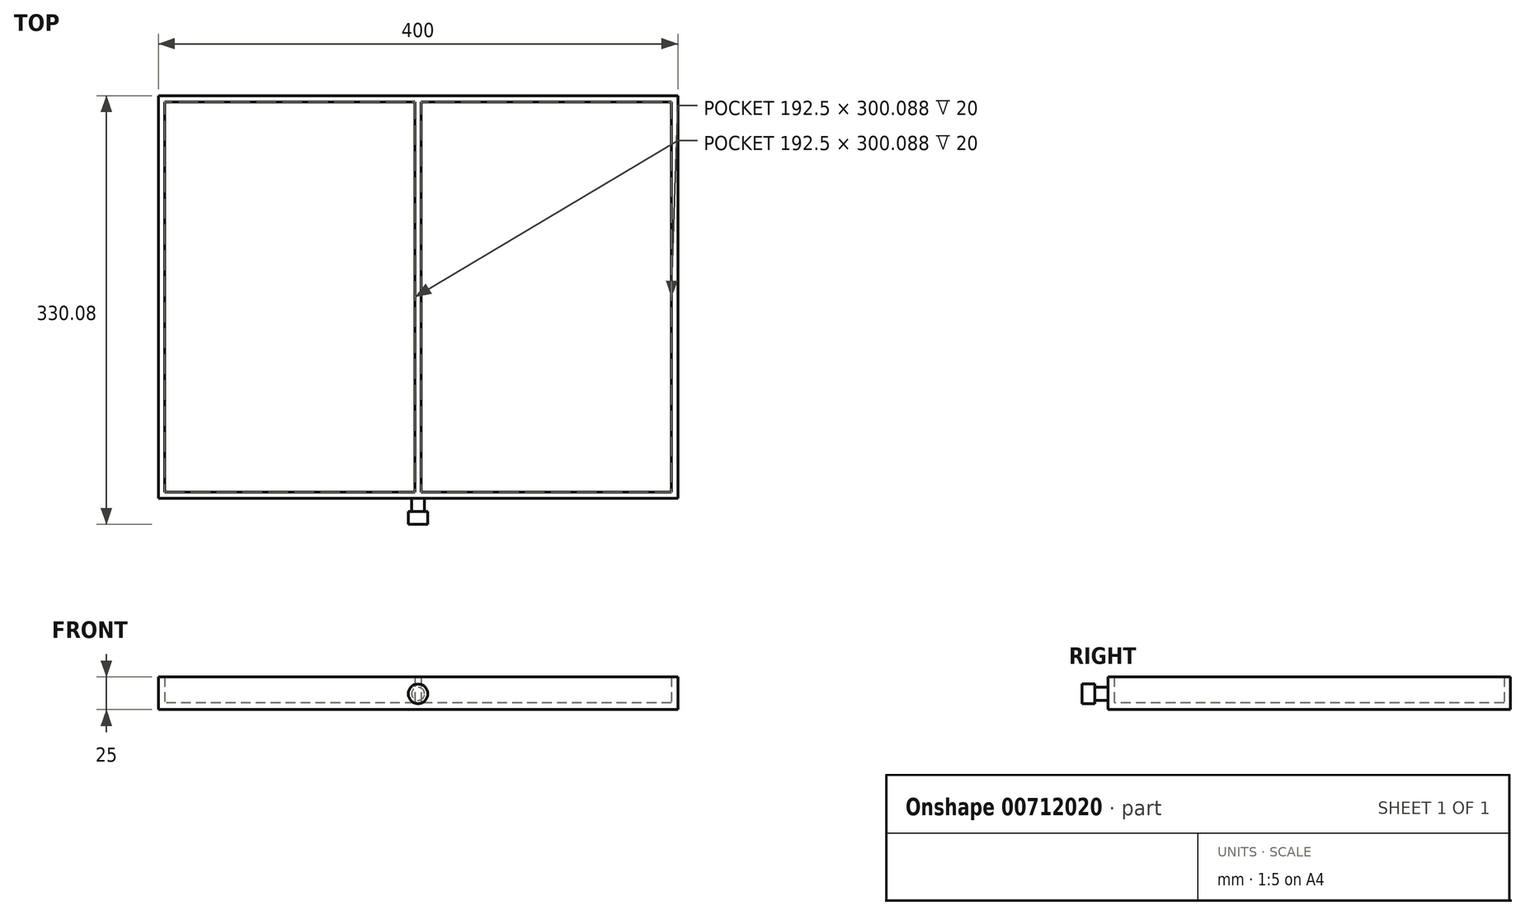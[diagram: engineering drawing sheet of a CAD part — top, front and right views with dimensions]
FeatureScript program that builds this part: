
annotation { "Feature Type Name" : "Feature", "Feature Type Description" : "" }
export const myFeature = defineFeature(function(context is Context, id is Id, definition is map)
    precondition{}
    {
        {
            var Q0;
            Q0=qCreatedBy(makeId("Top.planeOp"),FACE);
            var sketch = newSketch(context, id + "F0", { "sketchPlane" : qUnion([Q0])});
            skLineSegment(sketch, "E0.bottom", {"start": v(-33.22, 0) * mm, "end": v(5.14, 0) * mm});
            skLineSegment(sketch, "E0.top", {"start": v(-33.22, 42.2) * mm, "end": v(5.14, 42.2) * mm});
            skLineSegment(sketch, "E0.left", {"start": v(-33.22, 0) * mm, "end": v(-33.22, 42.2) * mm});
            skLineSegment(sketch, "E0.right", {"start": v(5.14, 0) * mm, "end": v(5.14, 42.2) * mm});
            skSolve(sketch);
        }
        {
            var Q0;
            Q0=makeQuery(id+"F0.imprint","IMPRINT",FACE,{"disambiguationData":[TD([[makeQuery(id+"F0.imprint","IMPRINT",EDGE,{"derivedFrom":sQuery(id+"F0.wireOp",EDGE,"E0.bottom")}),1.0]])]});
            extrude(context, id + "F1", {"entities" : qUnion([Q0]), "depth" : 0.69 * mm, "offsetDistance" : 25.4 * mm});
        }
        {
            var Q0;
            Q0=makeQuery(id+"F1.opExtrude","SWEPT_BODY",BODY,{"disambiguationData":[OSD([sQuery(id+"F0.wireOp",EDGE,"E0.bottom"),sQuery(id+"F0.wireOp",EDGE,"E0.top"),sQuery(id+"F0.wireOp",EDGE,"E0.left"),sQuery(id+"F0.wireOp",EDGE,"E0.right")])]});
            deleteBodies(context, id + "F2", {"entities" : qUnion([Q0])});
        }
        {
            var Q0;
            Q0=qCreatedBy(makeId("Top.planeOp"),FACE);
            var sketch = newSketch(context, id + "F3", { "sketchPlane" : qUnion([Q0])});
            skPoint(sketch, "E1.middle", {"position": v(0, 0) * mm});
            skLineSegment(sketch, "E2.bottom", {"start": v(200, -150.04) * mm, "end": v(-200, -150.04) * mm});
            skLineSegment(sketch, "E2.top", {"start": v(200, 150.04) * mm, "end": v(-200, 150.04) * mm});
            skLineSegment(sketch, "E2.left", {"start": v(200, -150.04) * mm, "end": v(200, 150.04) * mm});
            skLineSegment(sketch, "E2.right", {"start": v(-200, -150.04) * mm, "end": v(-200, 150.04) * mm});
            skSolve(sketch);
        }
        {
            var Q0;
            Q0=qSketchRegion(id+"F3",true);
            extrude(context, id + "F4", {"entities" : qUnion([Q0]), "depth" : 5 * mm, "offsetDistance" : 25 * mm});
        }
        {
            var Q0;
            Q0=makeQuery(id+"F4.opExtrude","CAP_FACE",FACE,{"disambiguationData":[OSD([sQuery(id+"F3.wireOp",EDGE,"E2.bottom"),sQuery(id+"F3.wireOp",EDGE,"E2.top"),sQuery(id+"F3.wireOp",EDGE,"E2.left"),sQuery(id+"F3.wireOp",EDGE,"E2.right")])],"isStart":false});
            var sketch = newSketch(context, id + "F5", { "sketchPlane" : qUnion([Q0])});
            skLineSegment(sketch, "E3.bottom", {"start": v(-200, -150.04) * mm, "end": v(-195, -150.04) * mm});
            skLineSegment(sketch, "E3.top", {"start": v(-200, 150.04) * mm, "end": v(-195, 150.04) * mm});
            skLineSegment(sketch, "E3.left", {"start": v(-200, -150.04) * mm, "end": v(-200, 150.04) * mm});
            skLineSegment(sketch, "E3.right", {"start": v(-195, -150.04) * mm, "end": v(-195, 150.04) * mm});
            skSolve(sketch);
        }
        {
            var Q0;
            Q0=qSketchRegion(id+"F5",true);
            extrude(context, id + "F6", {"entities" : qUnion([Q0]), "operationType" : NewBodyOperationType.ADD, "depth" : 20 * mm, "offsetDistance" : 25 * mm});
        }
        {
            var Q0;
            Q0=makeQuery(id+"F4.opExtrude","CAP_FACE",FACE,{"disambiguationData":[OSD([sQuery(id+"F3.wireOp",EDGE,"E2.bottom"),sQuery(id+"F3.wireOp",EDGE,"E2.top"),sQuery(id+"F3.wireOp",EDGE,"E2.left"),sQuery(id+"F3.wireOp",EDGE,"E2.right")])],"isStart":false});
            var sketch = newSketch(context, id + "F7", { "sketchPlane" : qUnion([Q0])});
            skLineSegment(sketch, "E4.bottom", {"start": v(200, 150.04) * mm, "end": v(195, 150.04) * mm});
            skLineSegment(sketch, "E4.top", {"start": v(200, -150.04) * mm, "end": v(195, -150.04) * mm});
            skLineSegment(sketch, "E4.left", {"start": v(200, 150.04) * mm, "end": v(200, -150.04) * mm});
            skLineSegment(sketch, "E4.right", {"start": v(195, 150.04) * mm, "end": v(195, -150.04) * mm});
            skSolve(sketch);
        }
        {
            var Q0;
            Q0=qSketchRegion(id+"F7",true);
            extrude(context, id + "F8", {"entities" : qUnion([Q0]), "operationType" : NewBodyOperationType.ADD, "depth" : 20 * mm, "offsetDistance" : 25 * mm});
        }
        {
            var Q0;
            Q0=makeQuery(id+"F8.boolean.opBoolean","MERGE",FACE,{"derivedFrom":[makeQuery(id+"F6.boolean.opBoolean","MERGE",FACE,{"derivedFrom":[makeQuery(id+"F4.opExtrude","SWEPT_FACE",FACE,{"disambiguationData":[OSD([sQuery(id+"F3.wireOp",EDGE,"E2.top")])]}),makeQuery(id+"F6.opExtrude","SWEPT_FACE",FACE,{"disambiguationData":[OSD([sQuery(id+"F5.wireOp",EDGE,"E3.top")])]})]}),makeQuery(id+"F8.opExtrude","SWEPT_FACE",FACE,{"disambiguationData":[OSD([sQuery(id+"F7.wireOp",EDGE,"E4.bottom")])]})]});
            var sketch = newSketch(context, id + "F9", { "sketchPlane" : qUnion([Q0])});
            skLineSegment(sketch, "E5.bottom", {"start": v(-200, 0) * mm, "end": v(200, 0) * mm});
            skLineSegment(sketch, "E5.top", {"start": v(-200, 25) * mm, "end": v(200, 25) * mm});
            skLineSegment(sketch, "E5.left", {"start": v(-200, 0) * mm, "end": v(-200, 25) * mm});
            skLineSegment(sketch, "E5.right", {"start": v(200, 0) * mm, "end": v(200, 25) * mm});
            skSolve(sketch);
        }
        {
            var Q0;
            Q0=qSketchRegion(id+"F9",true);
            extrude(context, id + "F10", {"entities" : qUnion([Q0]), "operationType" : NewBodyOperationType.ADD, "depth" : 5 * mm, "offsetDistance" : 25 * mm});
        }
        {
            var Q0;
            Q0=makeQuery(id+"F4.opExtrude","CAP_FACE",FACE,{"disambiguationData":[OSD([sQuery(id+"F3.wireOp",EDGE,"E2.bottom"),sQuery(id+"F3.wireOp",EDGE,"E2.top"),sQuery(id+"F3.wireOp",EDGE,"E2.left"),sQuery(id+"F3.wireOp",EDGE,"E2.right")])],"isStart":false});
            var sketch = newSketch(context, id + "F11", { "sketchPlane" : qUnion([Q0])});
            skLineSegment(sketch, "E6.bottom", {"start": v(-2.5, 150.04) * mm, "end": v(2.5, 150.04) * mm});
            skLineSegment(sketch, "E6.top", {"start": v(-2.5, -150.04) * mm, "end": v(2.5, -150.04) * mm});
            skLineSegment(sketch, "E6.left", {"start": v(-2.5, 150.04) * mm, "end": v(-2.5, -150.04) * mm});
            skLineSegment(sketch, "E6.right", {"start": v(2.5, 150.04) * mm, "end": v(2.5, -150.04) * mm});
            skPoint(sketch, "E7", {"position": v(0, 0) * mm});
            skLineSegment(sketch, "E8", {"start": v(0, 150.04) * mm, "end": v(0, -150.04) * mm, "construction": true});
            skSolve(sketch);
        }
        {
            var Q0;
            Q0=makeQuery(id+"F11.imprint","IMPRINT",FACE,{"disambiguationData":[TD([[makeQuery(id+"F11.imprint","IMPRINT",EDGE,{"derivedFrom":sQuery(id+"F11.wireOp",EDGE,"E6.bottom")}),1.0]])]});
            extrude(context, id + "F12", {"entities" : qUnion([Q0]), "operationType" : NewBodyOperationType.ADD, "depth" : 20 * mm, "offsetDistance" : 25 * mm});
        }
        {
            var Q0;
            Q0=makeQuery(id+"F12.boolean.opBoolean","MERGE",FACE,{"derivedFrom":[makeQuery(id+"F8.boolean.opBoolean","MERGE",FACE,{"derivedFrom":[makeQuery(id+"F6.boolean.opBoolean","MERGE",FACE,{"derivedFrom":[makeQuery(id+"F4.opExtrude","SWEPT_FACE",FACE,{"disambiguationData":[OSD([sQuery(id+"F3.wireOp",EDGE,"E2.bottom")])]}),makeQuery(id+"F6.opExtrude","SWEPT_FACE",FACE,{"disambiguationData":[OSD([sQuery(id+"F5.wireOp",EDGE,"E3.bottom")])]})]}),makeQuery(id+"F8.opExtrude","SWEPT_FACE",FACE,{"disambiguationData":[OSD([sQuery(id+"F7.wireOp",EDGE,"E4.top")])]})]}),makeQuery(id+"F12.opExtrude","SWEPT_FACE",FACE,{"disambiguationData":[OSD([sQuery(id+"F11.wireOp",EDGE,"E6.top")])]})]});
            var sketch = newSketch(context, id + "F13", { "sketchPlane" : qUnion([Q0])});
            skLineSegment(sketch, "E9.bottom", {"start": v(200, 0) * mm, "end": v(-200, 0) * mm});
            skLineSegment(sketch, "E9.top", {"start": v(200, 25) * mm, "end": v(-200, 25) * mm});
            skLineSegment(sketch, "E9.left", {"start": v(200, 0) * mm, "end": v(200, 25) * mm});
            skLineSegment(sketch, "E9.right", {"start": v(-200, 0) * mm, "end": v(-200, 25) * mm});
            skSolve(sketch);
        }
        {
            var Q0;
            Q0=qSketchRegion(id+"F13",true);
            extrude(context, id + "F14", {"entities" : qUnion([Q0]), "operationType" : NewBodyOperationType.ADD, "depth" : 5 * mm, "offsetDistance" : 25 * mm});
        }
        {
            var Q0;
            Q0=makeQuery(id+"F14.opExtrude","CAP_FACE",FACE,{"disambiguationData":[OSD([sQuery(id+"F13.wireOp",EDGE,"E9.bottom"),sQuery(id+"F13.wireOp",EDGE,"E9.top"),sQuery(id+"F13.wireOp",EDGE,"E9.left"),sQuery(id+"F13.wireOp",EDGE,"E9.right")])],"isStart":false});
            var sketch = newSketch(context, id + "F15", { "sketchPlane" : qUnion([Q0])});
            skCircle(sketch, "E10", {"center": v(0, 12.1) * mm, "radius": 5 * mm});
            skLineSegment(sketch, "E11", {"start": v(0, 25) * mm, "end": v(0, 0) * mm, "construction": true});
            skSolve(sketch);
        }
        {
            var Q0;
            Q0=makeQuery(id+"F15.imprint","IMPRINT",FACE,{"disambiguationData":[TD([[makeQuery(id+"F15.imprint","IMPRINT",EDGE,{"derivedFrom":sQuery(id+"F15.wireOp",EDGE,"E10")}),1.0]])]});
            extrude(context, id + "F16", {"entities" : qUnion([Q0]), "operationType" : NewBodyOperationType.ADD, "depth" : 10 * mm, "offsetDistance" : 25 * mm});
        }
        {
            var Q0;
            Q0=makeQuery(id+"F16.opExtrude","CAP_FACE",FACE,{"disambiguationData":[OSD([sQuery(id+"F15.wireOp",EDGE,"E10")])],"isStart":false});
            var sketch = newSketch(context, id + "F17", { "sketchPlane" : qUnion([Q0])});
            skCircle(sketch, "E12", {"center": v(0, 12.1) * mm, "radius": 7.5 * mm});
            skSolve(sketch);
        }
        {
            var Q0;
            Q0=makeQuery(id+"F17.imprint","IMPRINT",FACE,{"disambiguationData":[TD([[makeQuery(id+"F17.imprint","IMPRINT",EDGE,{"derivedFrom":sQuery(id+"F17.wireOp",EDGE,"E12")}),1.0]])]});
            var Q1;
            Q1=makeQuery(id+"F17.imprint","IMPRINT",FACE,{"disambiguationData":[TD([[makeQuery(id+"F17.imprint","IMPRINT",EDGE,{"derivedFrom":makeQuery(id+"F16.opExtrude","CAP_EDGE",EDGE,{"disambiguationData":[OSD([sQuery(id+"F15.wireOp",EDGE,"E10")])],"isStart":false})}),1.0]])]});
            extrude(context, id + "F18", {"entities" : qUnion([Q0, Q1]), "operationType" : NewBodyOperationType.ADD, "depth" : 10 * mm, "offsetDistance" : 25 * mm});
        }
    });
